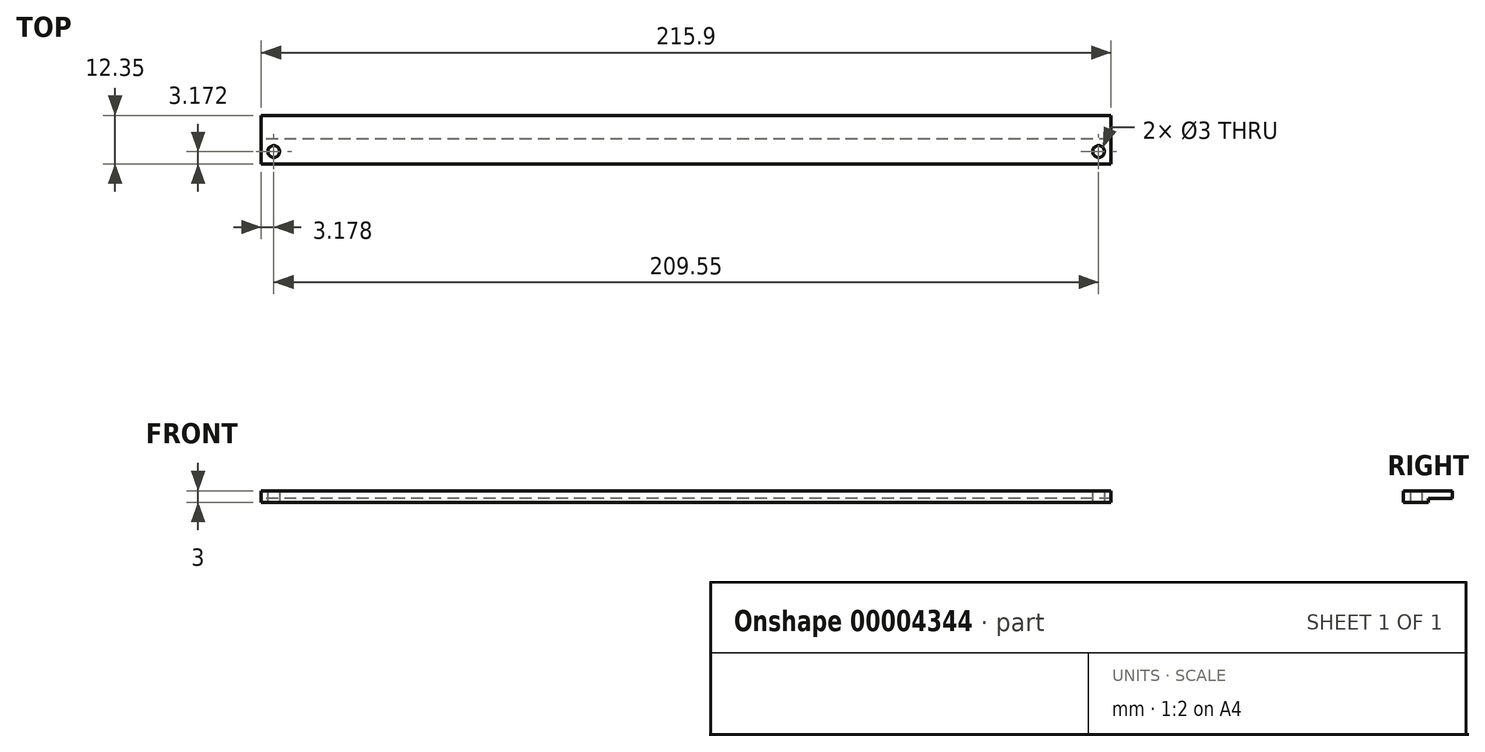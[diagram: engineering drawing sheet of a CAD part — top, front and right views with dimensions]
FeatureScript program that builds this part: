
annotation { "Feature Type Name" : "Feature", "Feature Type Description" : "" }
export const myFeature = defineFeature(function(context is Context, id is Id, definition is map)
    precondition{}
    {
        {
            var Q0;
            Q0=qCreatedBy(makeId("Top.planeOp"),FACE);
            var sketch = newSketch(context, id + "F0", { "sketchPlane" : qUnion([Q0])});
            skLineSegment(sketch, "E0.bottom", {"start": v(-212.27, -42.41) * mm, "end": v(3.63, -42.41) * mm});
            skLineSegment(sketch, "E0.top", {"start": v(-212.27, -54.76) * mm, "end": v(3.63, -54.76) * mm});
            skLineSegment(sketch, "E0.left", {"start": v(-212.27, -42.41) * mm, "end": v(-212.27, -54.76) * mm});
            skLineSegment(sketch, "E0.right", {"start": v(3.63, -42.41) * mm, "end": v(3.63, -54.76) * mm});
            skCircle(sketch, "E1", {"center": v(-209.1, -51.59) * mm, "radius": 1.5 * mm});
            skCircle(sketch, "E2", {"center": v(0.46, -51.59) * mm, "radius": 1.5 * mm});
            skSolve(sketch);
        }
        {
            var Q0;
            Q0=makeQuery(id+"F0.imprint","IMPRINT",FACE,{"disambiguationData":[TD([[makeQuery(id+"F0.imprint","IMPRINT",EDGE,{"derivedFrom":sQuery(id+"F0.wireOp",EDGE,"E0.bottom")}),-1.0]])]});
            extrude(context, id + "F1", {"entities" : qUnion([Q0]), "depth" : 3 * mm});
        }
        {
            var Q0;
            Q0=makeQuery(id+"F1.opExtrude","SWEPT_FACE",FACE,{"disambiguationData":[OSD([sQuery(id+"F0.wireOp",EDGE,"E0.left")])]});
            var sketch = newSketch(context, id + "F2", { "sketchPlane" : qUnion([Q0])});
            skLineSegment(sketch, "E3.bottom", {"start": v(42.41, 0) * mm, "end": v(48.41, 0) * mm});
            skLineSegment(sketch, "E3.top", {"start": v(42.41, 1) * mm, "end": v(48.41, 1) * mm});
            skLineSegment(sketch, "E3.left", {"start": v(42.41, 0) * mm, "end": v(42.41, 1) * mm});
            skLineSegment(sketch, "E3.right", {"start": v(48.41, 0) * mm, "end": v(48.41, 1) * mm});
            skSolve(sketch);
        }
        {
            var Q0;
            Q0=makeQuery(id+"F2.imprint","IMPRINT",FACE,{"disambiguationData":[TD([[makeQuery(id+"F2.imprint","IMPRINT",EDGE,{"derivedFrom":sQuery(id+"F2.wireOp",EDGE,"E3.bottom")}),1.0]])]});
            extrude(context, id + "F3", {"entities" : qUnion([Q0]), "operationType" : NewBodyOperationType.REMOVE, "endBound" : BoundingType.THROUGH_ALL, "oppositeDirection" : true, "depth" : 25.4 * mm});
        }
    });
